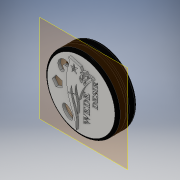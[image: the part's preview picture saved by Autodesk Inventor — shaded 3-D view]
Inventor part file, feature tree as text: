
AUTODESK INVENTOR PART (.ipt)
format: ipt  version: 2016 (Build 200138000, 138)  size: 1,013,248 bytes
history: native  units: in
note: dims shown in document units (in); Inventor stores cm internally (conversion verified against a paired STEP export)
features: extrude x18, sketch x16, fillet x3, plane x1, other x1
ambient origin geometry x8: Origin, YZ Plane, XZ Plane, XY Plane, X Axis, Y Axis, Z Axis, Center Point
bodies: Solid1 (feature_tree)
feature tree (39):
  extrude  "Extrusion1"  Depth=0.128in TaperAngle=0.0deg
  extrude  "Extrusion2"  Depth=0.3in TaperAngle=0.0deg
  sketch  "Sketch3"  dims[d3=2.65in d4=0.3in d5=0.0in d6=2.65in]
  fillet  "Fillet1"  Radius=2.65in
  extrude  "Extrusion3"  Depth=0.3in TaperAngle=0.0deg
  fillet  "Fillet2"  Radius=0.1in
  extrude  "Extrusion4"  Depth=0.046in TaperAngle=0.0deg
  extrude  "Extrusion5"  Depth=0.098in
  extrude  "Extrusion6"  Depth=0.2in
  extrude  "Extrusion7"  Depth=0.0844in
  extrude  "Extrusion11"  Depth=0.02in TaperAngle=0.0deg
  extrude  "Extrusion12"  Depth=0.085in
  extrude  "Extrusion13"  Depth=0.085in
  extrude  "Extrusion14"  Depth=0.1in TaperAngle=0.0deg
  fillet  "Fillet3"  Radius=0.6in
  extrude  "Extrusion15"  Depth=0.5in TaperAngle=0.0deg
  extrude  "Extrusion16"  Depth=1.5748in TaperAngle=360.0deg
  extrude  "Extrusion17"  Depth=0.4in TaperAngle=0.0deg
  plane  "Work Plane2"
  extrude  "Extrusion18"  Depth=0.17in
  extrude  "Extrusion19"  Depth=0.17in
  extrude  "Extrusion20"  Depth=0.01in TaperAngle=0.0deg
  extrude  "Extrusion21"  Depth=0.5in TaperAngle=0.0deg
  sketch  "Sketch1"  dims[d0=2.5in d1=0.128in d2=0.0in]
  sketch  "Sketch4"  dims[d7=0.1in d8=0.3in d9=0.0in d10=0.1in]
  sketch  "Sketch5"  dims[d11=0.093in d12=0.0in d13=0.046in d14=0.0in]
  sketch  "Sketch7"  dims[d15=0.285in d16=0.098in]
  sketch  "Sketch12"  dims[d17=0.3in d18=0.0in d19=0.2in]
  sketch  "Sketch16"  dims[d41=0.2835in d42=0.02in d43=0.0in]
  sketch  "Sketch17"  dims[d46=0.085in d48=0.085in]
  sketch  "Sketch20"  dims[d49=0.085in d50=0.085in]
  sketch  "Sketch21"  dims[d51=2.0in d52=0.0in d53=0.1in d54=0.0in d56=0.6in]
  sketch  "Sketch23"  dims[d60=2.3in d61=0.5in d62=0.0in]
  sketch  "Sketch24"  dims[d63=0.125in d64=1.5748in d66=360.0deg]
  sketch  "Sketch25"  dims[d68=1.5748in d70=360.0deg d72=0.4in d73=0.0in]
  other  "Image1"
  sketch  "Sketch26"  dims[d74=0.17in d75=0.17in]
  sketch  "Sketch28"  dims[d76=0.17in d77=0.17in d78=0.01in d79=0.0in d80=0.5in d81=0.0in d83=0.1in d84=0.0in d111=0.08in d112=0.0in d113=0.3in d114=0.0in d119=0.3in d120=0.0in]
  sketch  "Sketch13"  dims[d20=0.6in d21=0.0in d40=0.0844in]
